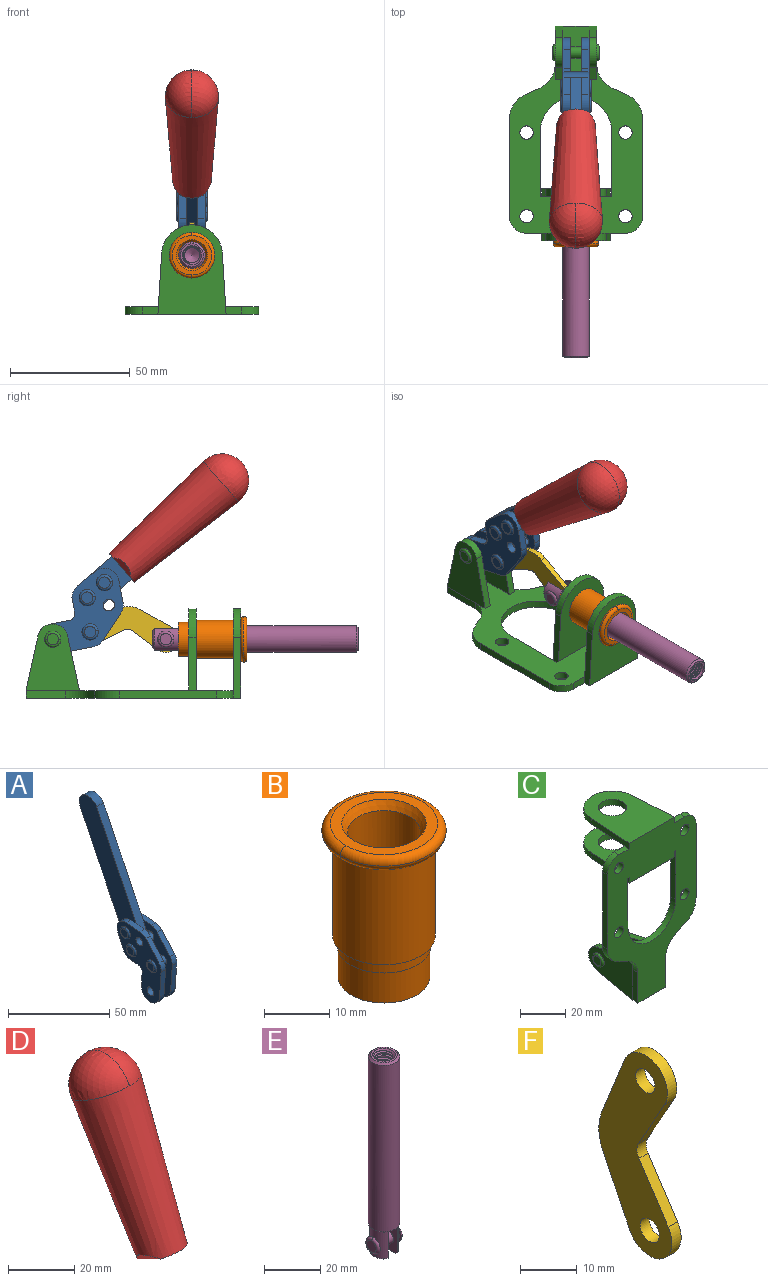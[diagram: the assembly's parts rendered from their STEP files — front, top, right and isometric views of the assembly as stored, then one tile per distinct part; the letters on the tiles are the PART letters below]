
ASSEMBLY  parts=6 mates=6
PART A: 59 faces, bbox 12.9x60.2x99.6 mm
  f0: torus R=2.39mm, axis (-1,0,0), area 14.9mm2, adj f20,f43,f51
  f1: torus R=2.39mm, axis (-1,0,0), area 14.9mm2, adj f19,f42,f51
  f2: torus R=2.39mm, axis (-1,0,0), area 14.9mm2, adj f18,f35,f51
  f3: torus R=2.39mm, axis (-1,0,0), area 14.9mm2, adj f14,f17,f23
  f4: torus R=2.39mm, axis (-1,0,0), area 14.9mm2, adj f13,f16,f23
  f5: torus R=2.39mm, axis (-1,0,0), area 14.9mm2, adj f12,f15,f23
  f6: cylinder r=2.39mm len=4.78mm, axis (1,0,0), area 46.5mm2, adj f48,f50,f51
  f7: cylinder r=2.39mm len=4.78mm, axis (1,0,0), area 46.5mm2, adj f50,f51
  f8: cylinder r=6.35mm len=12.68mm, axis (1,0,0), area 61.8mm2, adj f38,f39,f50,f51
  f9: cylinder r=2.39mm len=4.78mm, axis (-1,0,0), area 70.5mm2, adj f46,f50
  f10: cylinder r=2.39mm len=4.78mm, axis (-1,0,0), area 46.5mm2, adj f23,f45,f46
  f11: cylinder r=2.39mm len=4.78mm, axis (-1,0,0), area 46.5mm2, adj f23,f46
  f12: plane 4.78x4.78mm, normal (1,0,0), area 17.9mm2, adj f5,f15
  f13: plane 4.78x4.78mm, normal (1,0,0), area 17.9mm2, adj f4,f16
  f14: plane 4.78x4.78mm, normal (1,0,0), area 17.9mm2, adj f3,f17
  f15: torus R=2.39mm, axis (-1,0,0), area 14.9mm2, adj f5,f12,f23
  f16: torus R=2.39mm, axis (-1,0,0), area 14.9mm2, adj f4,f13,f23
  f17: torus R=2.39mm, axis (-1,0,0), area 14.9mm2, adj f3,f14,f23
  f18: plane 4.78x4.78mm, normal (-1,0,0), area 17.9mm2, adj f2,f35
  f19: plane 4.78x4.78mm, normal (-1,0,0), area 17.9mm2, adj f1,f42
  f20: plane 4.78x4.78mm, normal (-1,0,0), area 17.9mm2, adj f0,f43
  f21: plane 2.26x0.2mm, normal (1,0,0), area 0.2mm2, adj f31,f44
  f22: plane 2.26x0.2mm, normal (-1,0,0), area 0.2mm2, adj f41,f44
  f23: plane 39.37x30.77mm, normal (1,0,0), area 565.5mm2, adj f3,f4,f5,f10,f11,f15,f16,f17
  f24: cylinder r=6.1mm len=4.15mm, axis (-1,0,0), area 14.7mm2, adj f23,f25,f32,f46
  f25: plane 10.25x9.01mm, normal (0,-0.75,0.66), area 42.3mm2, adj f23,f24,f26,f46
  f26: cylinder r=6.35mm len=4.64mm, axis (-1,0,0), area 15.6mm2, adj f23,f25,f27,f46
  f27: plane 15.84x3.1mm, normal (0,-1,-0.07), area 49.2mm2, adj f23,f26,f28,f46
  f28: cylinder r=6.35mm len=12.68mm, axis (-1,0,0), area 61.8mm2, adj f23,f27,f29,f46
  f29: plane 8.11x3.1mm, normal (0,1,0.07), area 25.2mm2, adj f23,f28,f30,f46
  f30: cylinder r=3.05mm len=3.25mm, axis (-1,0,0), area 14.8mm2, adj f23,f29,f31,f46
  f31: plane 5.99x3.1mm, normal (0,0.07,-1), area 18.6mm2, adj f21,f23,f30,f44,f46
  f32: plane 9.5x3.1mm, normal (0,-0.07,1), area 29.5mm2, adj f23,f24,f33,f46,f47
  f33: cylinder r=6.1mm len=8.63mm, axis (-1,0,0), area 39.1mm2, adj f23,f32,f34,f47
  f34: plane 8.65x3.96mm, normal (0,0.91,-0.42), area 29.5mm2, adj f23,f33,f44,f47
  f35: torus R=2.39mm, axis (-1,0,0), area 14.9mm2, adj f2,f18,f51
  f36: plane 10.25x9.01mm, normal (0,-0.75,0.66), area 42.3mm2, adj f37,f49,f50,f51
  f37: cylinder r=6.35mm len=4.64mm, axis (1,0,0), area 15.6mm2, adj f36,f38,f50,f51
  f38: plane 15.84x3.1mm, normal (0,-1,-0.07), area 49.2mm2, adj f8,f37,f50,f51
  f39: plane 8.11x3.1mm, normal (0,1,0.07), area 25.2mm2, adj f8,f40,f50,f51
  f40: cylinder r=3.05mm len=3.25mm, axis (1,0,0), area 14.8mm2, adj f39,f41,f50,f51
  f41: plane 5.99x3.1mm, normal (0,0.07,-1), area 18.6mm2, adj f22,f40,f44,f50,f51
  f42: torus R=2.39mm, axis (-1,0,0), area 14.9mm2, adj f1,f19,f51
  f43: torus R=2.39mm, axis (-1,0,0), area 14.9mm2, adj f0,f20,f51
  f44: cylinder r=6.35mm len=12.12mm, axis (-1,0,0), area 128.9mm2, adj f21,f22,f23,f31,f34,f41,f46,f47
  f45: plane 2.65x1.35mm, normal (1,0,0), area 1mm2, adj f10,f55
  f46: plane 39.08x20.42mm, normal (-1,0,0), area 412.5mm2, adj f9,f10,f11,f24,f25,f26,f27,f28
  f47: plane 77.62x39.82mm, normal (1,0,0), area 850mm2, adj f32,f33,f34,f44,f53,f54,f55
  f48: plane 2.65x1.35mm, normal (-1,0,0), area 1mm2, adj f6,f55
  f49: cylinder r=6.1mm len=4.15mm, axis (1,0,0), area 14.7mm2, adj f36,f50,f51,f56
  f50: plane 39.08x20.42mm, normal (1,0,0), area 412.5mm2, adj f6,f7,f8,f9,f36,f37,f38,f39
  f51: plane 39.37x30.77mm, normal (-1,0,0), area 565.5mm2, adj f0,f1,f2,f6,f7,f8,f35,f36
  f52: plane 8.65x3.96mm, normal (0,0.91,-0.42), area 29.5mm2, adj f44,f51,f57,f58
  f53: plane 68.49x33.4mm, normal (0,0.9,-0.44), area 358.1mm2, adj f44,f47,f54,f58
  f54: cylinder r=6.35mm len=12.06mm, axis (1,0,0), area 93.7mm2, adj f47,f53,f55,f58
  f55: plane 68.49x33.4mm, normal (0,-0.9,0.44), area 358.1mm2, adj f44,f45,f46,f47,f48,f50,f54,f58
  f56: plane 9.5x3.1mm, normal (0,-0.07,1), area 29.5mm2, adj f49,f50,f51,f57,f58
  f57: cylinder r=6.1mm len=8.63mm, axis (1,0,0), area 39.1mm2, adj f51,f52,f56,f58
  f58: plane 77.62x39.82mm, normal (-1,0,0), area 850mm2, adj f44,f52,f53,f54,f55,f56,f57
PART B: 15 faces, bbox 20.6x20.6x28.7 mm
  f0: torus R=8.26mm, axis (0,0,1), area 56.8mm2, adj f1,f10,f12
  f1: torus R=8.26mm, axis (0,0,1), area 56.8mm2, adj f0,f6,f13
  f2: cylinder r=5.59mm len=25.91mm, axis (0,0,1), area 909.6mm2, adj f3,f4
  f3: cone r=6.86mm half-angle=45deg, axis (0,0,-1), area 70.2mm2, adj f2,f14
  f4: cone r=6.47mm half-angle=30deg, axis (0,0,1), area 66.7mm2, adj f2,f13
  f5: cylinder r=7.04mm len=14.07mm, axis (0,0,1), area 252.6mm2, adj f11,f14
  f6: torus R=8.26mm, axis (0,0,1), area 56.8mm2, adj f1,f12,f13
  f7: cylinder r=7.16mm len=14.33mm, axis (0,0,1), area 91.5mm2, adj f9,f11
  f8: cylinder r=7.86mm len=18.42mm, axis (0,0,1), area 909.6mm2, adj f9,f10
  f9: plane 15.72x15.72mm, normal (0,0,-1), area 33mm2, adj f7,f8
  f10: plane 16.51x16.51mm, normal (0,0,-1), area 19.9mm2, adj f0,f8,f12
  f11: plane 14.33x14.33mm, normal (0,0,-1), area 5.7mm2, adj f5,f7
  f12: torus R=8.26mm, axis (0,0,1), area 56.8mm2, adj f0,f6,f10
  f13: plane 16.51x16.51mm, normal (0,0,1), area 82.7mm2, adj f1,f4,f6
  f14: plane 14.07x14.07mm, normal (0,0,-1), area 7.8mm2, adj f3,f5
PART C: 55 faces, bbox 55.7x37.4x89.8 mm
  f0: torus R=2.41mm, axis (-1,0,0), area 15mm2, adj f11,f15,f25
  f1: torus R=2.41mm, axis (-1,0,0), area 15mm2, adj f10,f12,f22
  f2: cylinder r=2.78mm len=5.56mm, axis (0,-1,0), area 54.2mm2, adj f30,f54
  f3: cylinder r=14.99mm len=29.97mm, axis (0,-1,0), area 145.9mm2, adj f30,f49,f53,f54
  f4: cylinder r=2.78mm len=5.56mm, axis (0,-1,0), area 54.2mm2, adj f30,f54
  f5: cylinder r=2.78mm len=5.56mm, axis (0,-1,0), area 54.2mm2, adj f30,f54
  f6: cylinder r=2.78mm len=5.56mm, axis (0,-1,0), area 54.2mm2, adj f30,f54
  f7: cylinder r=6.35mm len=12.7mm, axis (0,0,1), area 123.6mm2, adj f27,f51
  f8: cylinder r=6.35mm len=12.7mm, axis (0,0,-1), area 124.7mm2, adj f21,f35
  f9: cylinder r=2.41mm len=11.18mm, axis (-1,0,0), area 169.4mm2, adj f16,f19
  f10: plane 4.83x4.83mm, normal (1,0,0), area 18.3mm2, adj f1,f12
  f11: plane 4.83x4.83mm, normal (-1,0,0), area 18.3mm2, adj f0,f15
  f12: torus R=2.41mm, axis (-1,0,0), area 15mm2, adj f1,f10,f22
  f13: cylinder r=6.35mm len=12.41mm, axis (1,0,0), area 53.4mm2, adj f18,f19,f22,f23
  f14: cylinder r=6.35mm len=12.41mm, axis (-1,0,0), area 53.4mm2, adj f16,f17,f24,f25
  f15: torus R=2.41mm, axis (-1,0,0), area 15mm2, adj f0,f11,f25
  f16: plane 27.86x22.35mm, normal (1,0,0), area 425.4mm2, adj f9,f14,f17,f24,f30
  f17: plane 22.86x4.97mm, normal (0,0.21,0.98), area 72.5mm2, adj f14,f16,f25,f30
  f18: plane 22.86x4.97mm, normal (0,0.21,0.98), area 72.5mm2, adj f13,f19,f22,f30
  f19: plane 27.86x22.35mm, normal (-1,0,0), area 425.4mm2, adj f9,f13,f18,f23,f30
  f20: cylinder r=12.7mm len=25.35mm, axis (0,0,-1), area 119.8mm2, adj f21,f34,f35,f36
  f21: plane 34.21x28.07mm, normal (0,0,-1), area 702.4mm2, adj f8,f20,f30,f34,f36
  f22: plane 27.96x22.45mm, normal (1,0,0), area 407.2mm2, adj f1,f12,f13,f18,f23,f30,f42,f43
  f23: plane 22.86x4.97mm, normal (0,0.21,-0.98), area 72.5mm2, adj f13,f19,f22,f44
  f24: plane 22.86x4.97mm, normal (0,0.21,-0.98), area 72.5mm2, adj f14,f16,f25,f44
  f25: plane 27.86x22.35mm, normal (-1,0,0), area 407.1mm2, adj f0,f14,f15,f17,f24,f30,f45,f46
  f26: plane 3.1x0.95mm, normal (0,0,-1), area 2.7mm2, adj f30,f49,f50,f54
  f27: plane 34.21x28.07mm, normal (0,0,1), area 702.4mm2, adj f7,f28,f30,f50,f52
  f28: cylinder r=12.7mm len=25.35mm, axis (0,0,1), area 118.8mm2, adj f27,f50,f51,f52
  f29: plane 3.1x0.95mm, normal (0,0,-1), area 2.7mm2, adj f30,f52,f53,f54
  f30: plane 86.54x55.63mm, normal (0,1,0), area 2362.9mm2, adj f2,f3,f4,f5,f6,f16,f17,f18
  f31: plane 40.56x3.1mm, normal (-1,0,0), area 125.7mm2, adj f30,f32,f48,f54
  f32: cylinder r=7.11mm len=7.11mm, axis (0,-1,0), area 34.6mm2, adj f30,f31,f33,f54
  f33: plane 6.67x3.1mm, normal (0,0,1), area 20.4mm2, adj f30,f32,f34,f54
  f34: plane 25.39x3.13mm, normal (-1,0.06,0), area 79.5mm2, adj f20,f21,f33,f35,f54
  f35: plane 37.31x28.45mm, normal (0,0,1), area 789.9mm2, adj f8,f20,f34,f36,f54
  f36: plane 25.39x3.13mm, normal (1,0.06,0), area 79.5mm2, adj f20,f21,f35,f37,f54
  f37: plane 6.67x3.1mm, normal (0,0,1), area 20.4mm2, adj f30,f36,f38,f54
  f38: cylinder r=7.11mm len=7.11mm, axis (0,-1,0), area 34.6mm2, adj f30,f37,f39,f54
  f39: plane 40.56x3.1mm, normal (1,0,0), area 125.7mm2, adj f30,f38,f40,f54
  f40: cylinder r=11.18mm len=10.16mm, axis (0,-1,0), area 39.5mm2, adj f30,f39,f41,f54
  f41: plane 6.09x3.1mm, normal (0.42,0,-0.91), area 20.8mm2, adj f30,f40,f42,f54
  f42: cylinder r=11.18mm len=9.41mm, axis (0,-1,0), area 37.2mm2, adj f22,f30,f41,f43,f54
  f43: plane 16.5x3.1mm, normal (1,0,0), area 51.1mm2, adj f22,f42,f44,f54
  f44: plane 17.37x3.1mm, normal (0,0,-1), area 53.8mm2, adj f23,f24,f30,f43,f45,f54
  f45: plane 16.5x3.1mm, normal (-1,0,0), area 51.1mm2, adj f25,f44,f46,f54
  f46: cylinder r=11.18mm len=9.41mm, axis (0,-1,0), area 37.2mm2, adj f25,f30,f45,f47,f54
  f47: plane 6.09x3.1mm, normal (-0.42,0,-0.91), area 20.8mm2, adj f30,f46,f48,f54
  f48: cylinder r=11.18mm len=10.16mm, axis (0,-1,0), area 39.5mm2, adj f30,f31,f47,f54
  f49: plane 26.54x3.1mm, normal (-1,0,0), area 82.3mm2, adj f3,f26,f30,f54
  f50: plane 25.39x3.1mm, normal (1,0.06,0), area 78.8mm2, adj f26,f27,f28,f51,f54
  f51: plane 37.31x28.45mm, normal (0,0,-1), area 789.9mm2, adj f7,f28,f50,f52,f54
  f52: plane 25.39x3.1mm, normal (-1,0.06,0), area 78.8mm2, adj f27,f28,f29,f51,f54
  f53: plane 26.54x3.1mm, normal (1,0,0), area 82.3mm2, adj f3,f29,f30,f54
  f54: plane 89.66x55.63mm, normal (0,-1,0), area 2678.5mm2, adj f2,f3,f4,f5,f6,f26,f29,f31
PART D: 11 faces, bbox 22.3x42.6x64.5 mm
  f0: sphere r=11.13mm, area 411.4mm2, adj f1,f8
  f1: cone r=11.11mm half-angle=3.3deg, axis (0,0.44,0.9), area 3251.8mm2, adj f0,f7,f8,f9,f10
  f2: cylinder r=6.16mm len=11.7mm, axis (1,0,0), area 89.5mm2, adj f3,f4,f5,f6
  f3: plane 60.23x36.75mm, normal (-1,0,0), area 763.6mm2, adj f2,f4,f6,f10
  f4: plane 51.37x25.05mm, normal (0,0.9,-0.44), area 264.2mm2, adj f2,f3,f5,f10
  f5: plane 60.23x36.75mm, normal (1,0,0), area 763.6mm2, adj f2,f4,f6,f10
  f6: plane 51.37x25.05mm, normal (0,-0.9,0.44), area 264.2mm2, adj f2,f3,f5,f10
  f7: plane 9.95x5.95mm, normal (0.71,-0.31,-0.64), area 25.8mm2, adj f1,f10
  f8: sphere r=11.13mm, area 411.4mm2, adj f0,f1
  f9: plane 9.95x5.95mm, normal (-0.71,-0.31,-0.64), area 25.8mm2, adj f1,f10
  f10: plane 14.27x11.38mm, normal (0,-0.44,-0.9), area 106.7mm2, adj f1,f3,f4,f5,f6,f7,f9
PART E: 48 faces, bbox 12.6x11.1x86.1 mm
  f0: torus R=2.41mm, axis (-1,0,0), area 15mm2, adj f30,f32,f34
  f1: torus R=2.41mm, axis (-1,0,0), area 15mm2, adj f29,f31,f33
  f2: cylinder r=5.54mm len=72.39mm, axis (0,0,1), area 2518.5mm2, adj f3,f4,f42,f43
  f3: cone r=5.54mm half-angle=45deg, axis (0,0,1), area 7.6mm2, adj f2,f5,f41
  f4: cone r=5.54mm half-angle=45deg, axis (0,0,-1), area 34.9mm2, adj f2,f39
  f5: cylinder r=5.08mm len=11.48mm, axis (0,0,1), area 108.3mm2, adj f3,f7,f8,f41
  f6: cylinder r=2.41mm len=4.83mm, axis (-1,0,0), area 71.2mm2, adj f40,f41
  f7: cylinder r=2.41mm len=4.83mm, axis (-1,0,0), area 7.6mm2, adj f5,f34
  f8: cone r=5.08mm half-angle=45deg, axis (0,0,1), area 10.6mm2, adj f5,f37,f41
  f9: cone r=3.98mm half-angle=45deg, axis (0,0,1), area 17.6mm2, adj f27,f39,f45,f46,f47
  f10: cylinder r=2.41mm len=4.83mm, axis (-1,0,0), area 7.6mm2, adj f33,f38
  f11: cylinder r=3.2mm len=6.4mm, axis (0,0,1), area 78.4mm2, adj f12,f28,f44,f45,f47
  f12: cylinder r=3.2mm len=6.4mm, axis (0,0,1), area 10.5mm2, adj f11,f13,f45,f47
  f13: cylinder r=3.2mm len=6.4mm, axis (0,0,1), area 10.5mm2, adj f12,f14,f45,f47
  f14: cylinder r=3.2mm len=6.4mm, axis (0,0,1), area 10.5mm2, adj f13,f15,f45,f47
  f15: cylinder r=3.2mm len=6.4mm, axis (0,0,1), area 10.5mm2, adj f14,f16,f45,f47
  f16: cylinder r=3.2mm len=6.4mm, axis (0,0,1), area 10.5mm2, adj f15,f17,f45,f47
  f17: cylinder r=3.2mm len=6.4mm, axis (0,0,1), area 10.5mm2, adj f16,f18,f45,f47
  f18: cylinder r=3.2mm len=6.4mm, axis (0,0,1), area 10.5mm2, adj f17,f19,f45,f47
  f19: cylinder r=3.2mm len=6.4mm, axis (0,0,1), area 10.5mm2, adj f18,f20,f45,f47
  f20: cylinder r=3.2mm len=6.4mm, axis (0,0,1), area 10.5mm2, adj f19,f21,f45,f47
  f21: cylinder r=3.2mm len=6.4mm, axis (0,0,1), area 10.5mm2, adj f20,f22,f45,f47
  f22: cylinder r=3.2mm len=6.4mm, axis (0,0,1), area 10.5mm2, adj f21,f23,f45,f47
  f23: cylinder r=3.2mm len=6.4mm, axis (0,0,1), area 10.5mm2, adj f22,f24,f45,f47
  f24: cylinder r=3.2mm len=6.4mm, axis (0,0,1), area 10.5mm2, adj f23,f25,f45,f47
  f25: cylinder r=3.2mm len=6.4mm, axis (0,0,1), area 10.5mm2, adj f24,f26,f45,f47
  f26: cylinder r=3.2mm len=6.4mm, axis (0,0,1), area 10.5mm2, adj f25,f27,f45,f47
  f27: cylinder r=3.2mm len=6.4mm, axis (0,0,1), area 7.4mm2, adj f9,f26,f45,f47
  f28: cone r=3.2mm half-angle=60deg, axis (0,0,1), area 37.2mm2, adj f11
  f29: plane 4.83x4.83mm, normal (-1,0,0), area 18.3mm2, adj f1,f31
  f30: plane 4.83x4.83mm, normal (1,0,0), area 18.3mm2, adj f0,f32
  f31: torus R=2.41mm, axis (-1,0,0), area 15mm2, adj f1,f29,f33
  f32: torus R=2.41mm, axis (-1,0,0), area 15mm2, adj f0,f30,f34
  f33: plane 6.83x6.83mm, normal (1,0,0), area 18.3mm2, adj f1,f10,f31
  f34: plane 6.83x6.83mm, normal (-1,0,0), area 18.3mm2, adj f0,f7,f32
  f35: cone r=5.08mm half-angle=45deg, axis (0,0,1), area 10.6mm2, adj f36,f38,f40
  f36: plane 7.25x1.97mm, normal (0,0,-1), area 10mm2, adj f35,f40
  f37: plane 7.25x1.97mm, normal (0,0,-1), area 10mm2, adj f8,f41
  f38: cylinder r=5.08mm len=11.48mm, axis (0,0,1), area 108.3mm2, adj f10,f35,f40,f42
  f39: plane 9.55x9.55mm, normal (0,0,1), area 22mm2, adj f4,f9
  f40: plane 12.76x10.09mm, normal (1,0,0), area 95.7mm2, adj f6,f35,f36,f38,f42,f43
  f41: plane 12.76x10.09mm, normal (-1,0,0), area 95.7mm2, adj f3,f5,f6,f8,f37,f43
  f42: cone r=5.54mm half-angle=45deg, axis (0,0,1), area 7.6mm2, adj f2,f38,f40
  f43: plane 11.07x4.7mm, normal (0,0,-1), area 50.4mm2, adj f2,f40,f41
  f44: plane 0.89x0.62mm, normal (-1,0,0), area 0.3mm2, adj f11,f45,f46,f47
  f45: bspline ~24.8x7.63mm, area 266.6mm2, adj f9,f11,f12,f13,f14,f15,f16,f17
  f46: bspline ~24.87x7.63mm, area 73.6mm2, adj f9,f44,f45,f47
  f47: bspline ~24.98x7.63mm, area 272.5mm2, adj f9,f11,f12,f13,f14,f15,f16,f17
PART F: 12 faces, bbox 2.3x18.2x42.8 mm
  f0: cylinder r=2.4mm len=4.8mm, axis (1,0,0), area 34.9mm2, adj f4,f11
  f1: cylinder r=10.41mm len=8.47mm, axis (1,0,0), area 20.2mm2, adj f4,f9,f10,f11
  f2: cylinder r=3.05mm len=3.16mm, axis (1,0,0), area 7.7mm2, adj f4,f6,f7,f11
  f3: cylinder r=2.4mm len=4.8mm, axis (1,0,0), area 34.9mm2, adj f4,f11
  f4: plane 42.81x18.23mm, normal (-1,0,0), area 414.1mm2, adj f0,f1,f2,f3,f5,f6,f7,f8
  f5: cylinder r=5.54mm len=10.67mm, axis (1,0,0), area 41.8mm2, adj f4,f6,f10,f11
  f6: plane 11.66x6.53mm, normal (0,-0.87,-0.49), area 30.9mm2, adj f2,f4,f5,f11
  f7: plane 11.17x7.33mm, normal (0,-0.84,0.55), area 30.9mm2, adj f2,f4,f8,f11
  f8: cylinder r=5.54mm len=10.51mm, axis (1,0,0), area 41.8mm2, adj f4,f7,f9,f11
  f9: plane 13.67x6.67mm, normal (0,0.9,-0.44), area 35.1mm2, adj f1,f4,f8,f11
  f10: plane 14.1x5.7mm, normal (0,0.93,0.37), area 35.1mm2, adj f1,f4,f5,f11
  f11: plane 42.81x18.23mm, normal (1,0,0), area 414.1mm2, adj f0,f1,f2,f3,f5,f6,f7,f8
PLACE A rot(axis=(1,0,0),75deg) t=(0,4.15,9.14)mm
PLACE B rot(axis=(0.58,0.58,-0.58),120deg) t=(-24.61,9.43,24.61)mm
PLACE C rot(axis=(1,0,0),90deg) t=(0,9.43,0)mm fixed
PLACE D rot(axis=(1,0,0),75deg) t=(-0.04,4.15,9.14)mm
PLACE E rot(axis=(1,0,0),90deg) t=(0,9.81,0)mm
PLACE F rot(axis=(0,-0.69,-0.73),180deg) t=(0,11.99,2.14)mm
MATE slider E.f2 <-> C.f7  axis (0,-1,0) through (0,-48.97,24.61)mm
MATE fastened D.f2 <-> A.f54  axis (1,0,0) through (-2.35,-30.37,91.94)mm
MATE fastened B.f2 <-> C.f7  axis (0,1,0) through (0,-36.96,24.61)mm
MATE revolute F.f5 <-> A.f4  axis (-1,0,0) through (0,25.94,27.64)mm
MATE revolute C.f0 <-> A.f7  axis (-1,0,0) through (0,41.52,24.61)mm
MATE revolute F.f3 <-> E.f6  axis (-1,0,0) through (0,-5.67,24.61)mm
